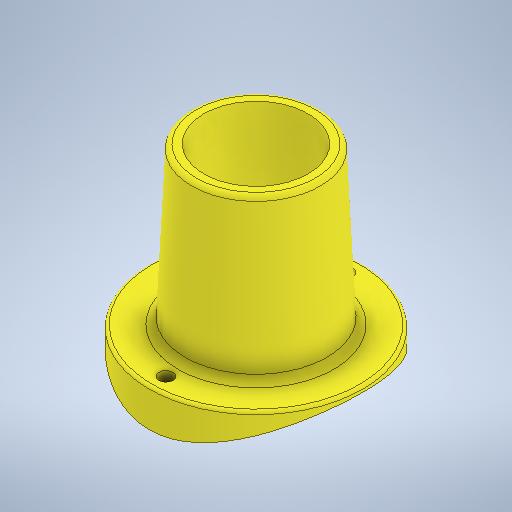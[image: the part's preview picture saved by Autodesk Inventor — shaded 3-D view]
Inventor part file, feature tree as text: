
AUTODESK INVENTOR PART (.ipt)
format: ipt  version: 2025.1 (Build 291241000, 241)  size: 322,560 bytes
history: native  units: mm
features: sketch x6, fillet x3, extrude x2, plane x2, hole x2, revolve x1, projected_geometry x1
ambient origin geometry x8: Origin, YZ Plane, XZ Plane, XY Plane, X Axis, Y Axis, Z Axis, Center Point
bodies: Solid1 (feature_tree)
feature tree (17):
  extrude  "Extrusion1"  Depth=8.0mm TaperAngle=0.0deg
  plane  "Work Plane1"
  revolve  "Revolution1"  [1 undecoded]
  fillet  "Fillet1"  Radius=33.0mm
  extrude  "Extrusion2"  TaperAngle=90.0deg  [1 undecoded]
  fillet  "Fillet2"  Radius=1.5mm
  fillet  "Fillet3"  Radius=81.0mm
  hole  "Hole2"  [1 undecoded]
  hole  "Hole3"  [1 undecoded]
  plane  "Work Plane2"
  sketch  "Sketch9"  dims[d27=19.0mm d28=19.0mm d29=3.0mm d30=6.0mm d31=22.0mm d32=27.0mm d33=90.0deg d34=8.0mm d35=0.0mm d36=1.0mm d37=0.0mm d39=45.0mm]
  sketch  "Sketch1"  dims[d0=45.0mm d1=8.0mm d2=0.0mm]
  sketch  "Sketch3"  dims[d3=0.0mm d4=27.0mm d5=33.0mm]
  projected_geometry  "Projected Loop1"
  sketch  "Sketch5"  dims[d6=30.0mm d7=90.0deg d8=1.5mm d16=81.0mm]
  sketch  "Sketch6"  dims[d17=45.0mm d18=0.0mm]
  sketch  "Sketch7"  dims[d19=20.0mm d20=6.0mm d21=22.0mm d22=27.0mm d23=90.0deg d24=8.0mm d25=0.0mm d26=0.6mm]
note: 4 required parameter values undecoded (feature->parameter linkage not recoverable at this tier; creation-order binding heuristic only, values carry confidence <= 0.55)